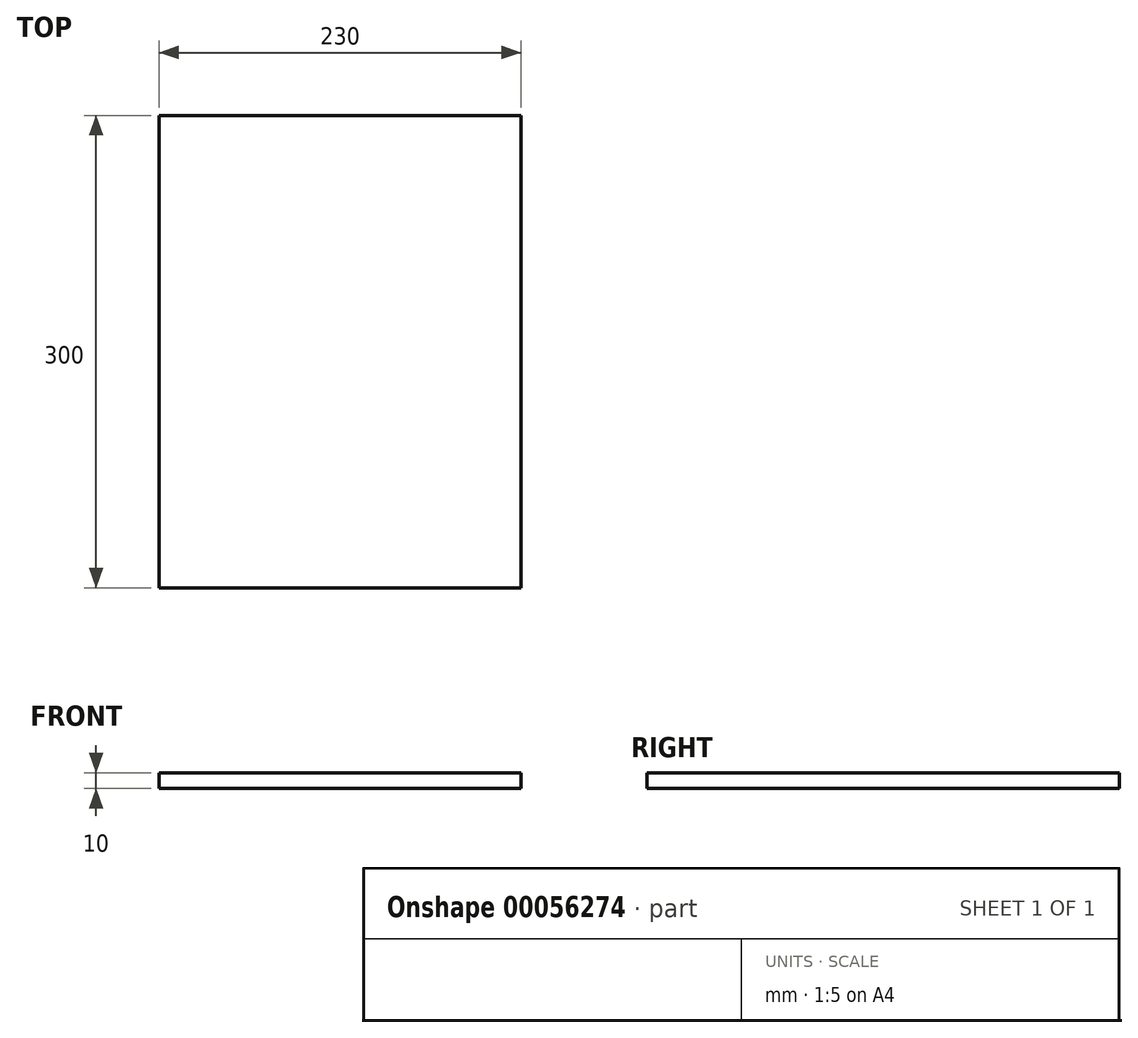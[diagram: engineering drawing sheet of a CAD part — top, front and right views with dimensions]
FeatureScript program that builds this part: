
annotation { "Feature Type Name" : "Feature", "Feature Type Description" : "" }
export const myFeature = defineFeature(function(context is Context, id is Id, definition is map)
    precondition{}
    {
        {
            var Q0;
            Q0=qCreatedBy(makeId("Top.planeOp"),FACE);
            var sketch = newSketch(context, id + "F0", { "sketchPlane" : qUnion([Q0])});
            skLineSegment(sketch, "E0.bottom", {"start": v(-44.88, 158.19) * mm, "end": v(185.12, 158.19) * mm});
            skLineSegment(sketch, "E0.top", {"start": v(-44.88, -141.81) * mm, "end": v(185.12, -141.81) * mm});
            skLineSegment(sketch, "E0.left", {"start": v(-44.88, 158.19) * mm, "end": v(-44.88, -141.81) * mm});
            skLineSegment(sketch, "E0.right", {"start": v(185.12, 158.19) * mm, "end": v(185.12, -141.81) * mm});
            skSolve(sketch);
        }
        {
            var Q0;
            Q0=qSketchRegion(id+"F0",true);
            extrude(context, id + "F1", {"entities" : qUnion([Q0]), "depth" : 10 * mm});
        }
    });
